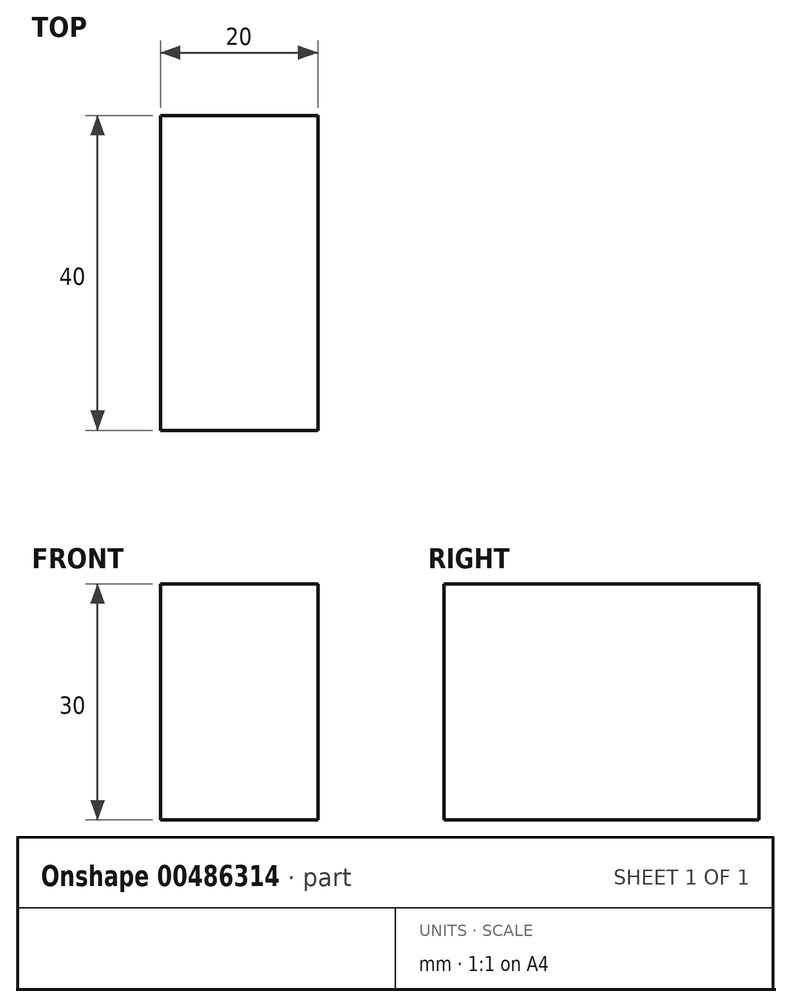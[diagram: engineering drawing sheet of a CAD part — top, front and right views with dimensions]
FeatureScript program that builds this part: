
annotation { "Feature Type Name" : "Feature", "Feature Type Description" : "" }
export const myFeature = defineFeature(function(context is Context, id is Id, definition is map)
    precondition{}
    {
        {
            var Q0;
            Q0=qCreatedBy(makeId("Top.planeOp"),FACE);
            var sketch = newSketch(context, id + "F0", { "sketchPlane" : qUnion([Q0])});
            skLineSegment(sketch, "E0", {"start": v(-43.7, 40) * mm, "end": v(-43.7, 0) * mm});
            skLineSegment(sketch, "E1", {"start": v(-43.7, 0) * mm, "end": v(-23.7, 0) * mm});
            skLineSegment(sketch, "E2", {"start": v(-23.7, 0) * mm, "end": v(-23.7, 40) * mm});
            skLineSegment(sketch, "E3", {"start": v(-23.7, 40) * mm, "end": v(-43.7, 40) * mm});
            skLineSegment(sketch, "E4", {"start": v(-23.7, 0) * mm, "end": v(16.3, 0) * mm});
            skLineSegment(sketch, "E5", {"start": v(16.3, 0) * mm, "end": v(16.3, 10) * mm});
            skLineSegment(sketch, "E6", {"start": v(16.3, 10) * mm, "end": v(16.3, 30) * mm});
            skLineSegment(sketch, "E7", {"start": v(16.3, 30) * mm, "end": v(16.3, 40) * mm});
            skLineSegment(sketch, "E8", {"start": v(16.3, 40) * mm, "end": v(-3.7, 40) * mm});
            skLineSegment(sketch, "E9", {"start": v(-3.7, 40) * mm, "end": v(-23.7, 40) * mm});
            skLineSegment(sketch, "E10", {"start": v(-3.7, 40) * mm, "end": v(-3.7, 30) * mm});
            skLineSegment(sketch, "E11", {"start": v(-3.7, 30) * mm, "end": v(16.3, 30) * mm});
            skLineSegment(sketch, "E12", {"start": v(-3.7, 30) * mm, "end": v(-23.7, 30) * mm});
            skLineSegment(sketch, "E13", {"start": v(16.3, 10) * mm, "end": v(-3.7, 10) * mm});
            skLineSegment(sketch, "E14", {"start": v(-3.7, 10) * mm, "end": v(-23.7, 10) * mm});
            skLineSegment(sketch, "E15", {"start": v(-3.7, 10) * mm, "end": v(-3.7, 0) * mm});
            skSolve(sketch);
        }
        {
            var Q0;
            Q0=makeQuery(id+"F0.imprint","IMPRINT",FACE,{"disambiguationData":[TD([[makeQuery(id+"F0.imprint","IMPRINT",EDGE,{"derivedFrom":sQuery(id+"F0.wireOp",EDGE,"E0")}),1.0]])]});
            extrude(context, id + "F1", {"entities" : qUnion([Q0]), "depth" : 30 * mm});
        }
    });
